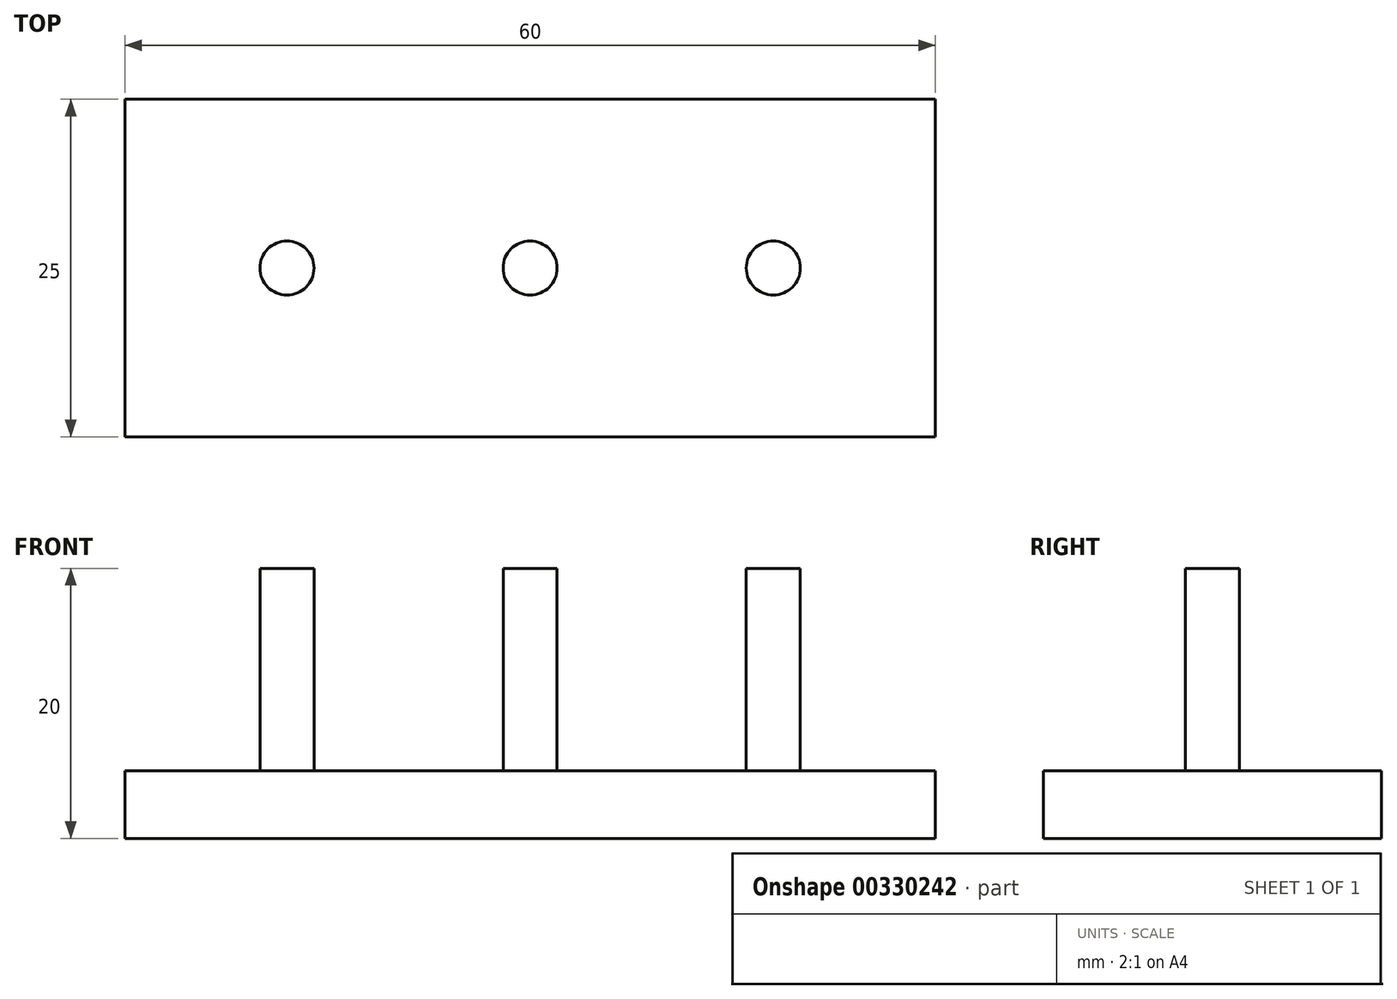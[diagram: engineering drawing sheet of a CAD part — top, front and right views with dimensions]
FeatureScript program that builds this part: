
annotation { "Feature Type Name" : "Feature", "Feature Type Description" : "" }
export const myFeature = defineFeature(function(context is Context, id is Id, definition is map)
    precondition{}
    {
        {
            var Q0;
            Q0=qCreatedBy(makeId("Top.planeOp"),FACE);
            var sketch = newSketch(context, id + "F0", { "sketchPlane" : qUnion([Q0])});
            skLineSegment(sketch, "E0.bottom", {"start": v(30, -12.5) * mm, "end": v(-30, -12.5) * mm});
            skLineSegment(sketch, "E0.top", {"start": v(30, 12.5) * mm, "end": v(-30, 12.5) * mm});
            skLineSegment(sketch, "E0.left", {"start": v(30, -12.5) * mm, "end": v(30, 12.5) * mm});
            skLineSegment(sketch, "E0.right", {"start": v(-30, -12.5) * mm, "end": v(-30, 12.5) * mm});
            skPoint(sketch, "E0.middle", {"position": v(0, 0) * mm});
            skSolve(sketch);
        }
        {
            var Q0;
            Q0 = qSketchRegion(id + "F0", true);
            extrude(context, id + "F1", {"entities" : qUnion([Q0]), "depth" : 5 * mm});
        }
        {
            var Q0;
            Q0=makeQuery(id+"F1.opExtrude","CAP_FACE",FACE,{"disambiguationData":[OSD([sQuery(id+"F0.wireOp",EDGE,"E0.bottom"),sQuery(id+"F0.wireOp",EDGE,"E0.top"),sQuery(id+"F0.wireOp",EDGE,"E0.left"),sQuery(id+"F0.wireOp",EDGE,"E0.right")])],"isStart":false});
            var sketch = newSketch(context, id + "F2", { "sketchPlane" : qUnion([Q0])});
            skCircle(sketch, "E1", {"center": v(-18, 0) * mm, "radius": 2 * mm});
            skCircle(sketch, "E2", {"center": v(0, 0) * mm, "radius": 2 * mm});
            skCircle(sketch, "E3", {"center": v(20, 0) * mm, "radius": 2 * mm});
            skSolve(sketch);
        }
        {
            var Q0;
            Q0=makeQuery(id+"F2.imprint","IMPRINT",FACE,{"disambiguationData":[TD([[makeQuery(id+"F2.imprint","IMPRINT",EDGE,{"derivedFrom":sQuery(id+"F2.wireOp",EDGE,"E2")}),1.0]])]});
            var Q1;
            Q1=sQuery(id+"F2.wireOp",EDGE,"E2");
            extrude(context, id + "F3", {"entities" : qUnion([Q0]), "surfaceEntities" : qUnion([Q1]), "depth" : 15 * mm});
        }
        {
            var Q0;
            Q0=makeQuery(id+"F1.opExtrude","CAP_FACE",FACE,{"disambiguationData":[OSD([sQuery(id+"F0.wireOp",EDGE,"E0.bottom"),sQuery(id+"F0.wireOp",EDGE,"E0.top"),sQuery(id+"F0.wireOp",EDGE,"E0.left"),sQuery(id+"F0.wireOp",EDGE,"E0.right")])],"isStart":false});
            var sketch = newSketch(context, id + "F4", { "sketchPlane" : qUnion([Q0])});
            skCircle(sketch, "E4", {"center": v(18, 0) * mm, "radius": 2 * mm});
            skSolve(sketch);
        }
        {
            var Q0;
            Q0 = qSketchRegion(id + "F4", true);
            extrude(context, id + "F5", {"entities" : qUnion([Q0]), "operationType" : NewBodyOperationType.ADD, "depth" : 15 * mm});
        }
        {
            var Q0;
            Q0 = qSketchRegion(id + "F4", true);
            extrude(context, id + "F6", {"entities" : qUnion([Q0]), "operationType" : NewBodyOperationType.ADD, "depth" : 15 * mm});
        }
        {
            var Q0;
            Q0=makeQuery(id+"F1.opExtrude","CAP_FACE",FACE,{"disambiguationData":[OSD([sQuery(id+"F0.wireOp",EDGE,"E0.bottom"),sQuery(id+"F0.wireOp",EDGE,"E0.top"),sQuery(id+"F0.wireOp",EDGE,"E0.left"),sQuery(id+"F0.wireOp",EDGE,"E0.right")])],"isStart":false});
            var sketch = newSketch(context, id + "F7", { "sketchPlane" : qUnion([Q0])});
            skCircle(sketch, "E5", {"center": v(-18, 0) * mm, "radius": 2 * mm});
            skSolve(sketch);
        }
        {
            var Q0;
            Q0 = qSketchRegion(id + "F7", true);
            extrude(context, id + "F8", {"entities" : qUnion([Q0]), "operationType" : NewBodyOperationType.ADD, "depth" : 15 * mm});
        }
    });
